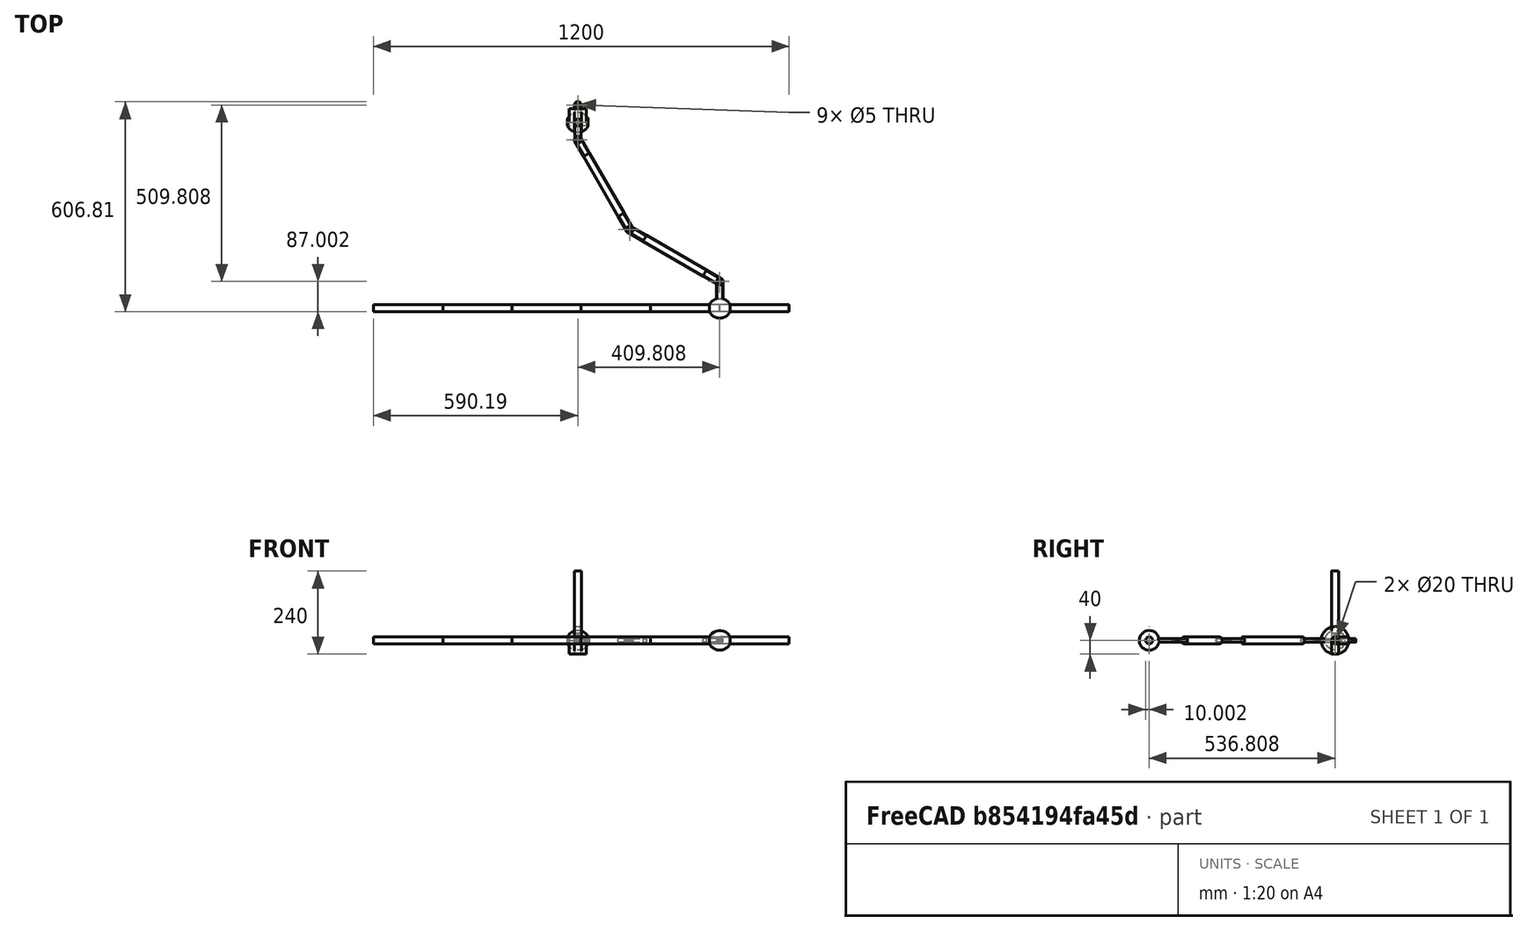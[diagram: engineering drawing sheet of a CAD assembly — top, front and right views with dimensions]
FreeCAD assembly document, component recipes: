
FREECAD ASSEMBLY — COMPONENT RECIPES ("Demo4Rev-Rev")

This assembly document has 7 components, labeled P0..P6 below (a component is one placed body or linked part). 7 of them carry a construction recipe — the FreeCAD feature program that regenerates the part from scratch, quoted from this document or its linked companion documents; the rest are supplied as boundary geometry only. No exploded tour is included for this assembly.
COMPONENT P0 — recipe-attached ("Weight", modeled in this document).
Construction recipe (the document's own serialized feature program — sketch geometry with constraints, then the solid features built on it; lengths are millimeters unless a unit is written):

FEATURE [Sketcher::SketchObject] Sketch
  FullyConstrained = true
  MapMode = 5
  Support = -> [XY_Plane]
  sketch-geometry (2):
    g0: LineSegment StartX=-30 StartY=10 StartZ=0 EndX=30 EndY=10 EndZ=0
    g1: ArcOfCircle CenterX=0 CenterY=-5 CenterZ=0 NormalX=0 NormalY=0 NormalZ=1 AngleXU=0 Radius=33.541 StartAngle=0.463648 EndAngle=2.67795
  constraints (7):
    c: Horizontal(g0)
    c: DistanceY(g-1,g0) = 10
    c: DistanceX(g-1,g0) = 30
    c: PointOnObject(g1,g-2)
    c: DistanceY(g1,g-1) = 5
    c: Coincident(g1,g0)
    c: Coincident(g1,g0)
FEATURE [PartDesign::Revolution] Revolution
  Angle = 360
  Axis = (1,0,0)
  Base = (0,0,0)
  Profile = -> Sketch
  ReferenceAxis = -> Sketch [H_Axis]
FEATURE [PartDesign::CoordinateSystem] WeightTop
  AttacherType = Attacher::AttachEngine3D
  MapMode = 11
  Placement = pos=(30,-1.8e-15,0) rot=(0.707107,0,0.707107;3.14159rad)
  Support = -> [Revolution]
FEATURE [PartDesign::CoordinateSystem] WeightBot
  AttacherType = Attacher::AttachEngine3D
  MapMode = 11
  Placement = pos=(-30,0,0) rot=(0.707107,0,0.707107;3.14159rad)
  Support = -> [Revolution]
FEATURE [PartDesign::CoordinateSystem] WeightLCS
  AttacherType = Attacher::AttachEngine3D
  MapMode = 2
  Support = -> [Body003]
FEATURE [PartDesign::Body] Body  label="Weight"
  Group = -> [Sketch,Revolution,WeightLCS,WeightTop,WeightBot]
  Origin = -> Origin
  Tip = -> Revolution
COMPONENT P1 — recipe-attached ("Rod", modeled in this document).
Construction recipe (the document's own serialized feature program — sketch geometry with constraints, then the solid features built on it; lengths are millimeters unless a unit is written):

FEATURE [Sketcher::SketchObject] Sketch001
  FullyConstrained = true
  MapMode = 5
  Support = -> [XY_Plane001]
  sketch-geometry (1):
    g0: Circle CenterX=0 CenterY=0 CenterZ=0 NormalX=0 NormalY=0 NormalZ=1 AngleXU=0 Radius=10
  constraints (2):
    c: Coincident(g0,g-1)
    c: Diameter(g0) = 20
FEATURE [PartDesign::Pad] Pad
  Direction = (0,0,1)
  Length = 200
  Length2 = 10
  Profile = -> Sketch001
  ReferenceAxis = -> Sketch001 [N_Axis]
  Type = 0
FEATURE [PartDesign::CoordinateSystem] RodTop
  AttacherType = Attacher::AttachEngine3D
  MapMode = 11
  Placement = pos=(0,0,200) rot=(0,0,1;1.5708rad)
  Support = -> [Pad]
FEATURE [PartDesign::CoordinateSystem] RodBottom
  AttacherType = Attacher::AttachEngine3D
  MapMode = 11
  Placement = pos=(0,0,0) rot=(0,0,1;1.5708rad)
  Support = -> [Pad]
FEATURE [PartDesign::Body] Body001  label="Rod"
  Group = -> [Sketch001,Pad,RodTop,RodBottom]
  Origin = -> Origin001
  Tip = -> Pad
COMPONENT P2 — recipe-attached ("LugBody", modeled in this document).
Construction recipe (the document's own serialized feature program — sketch geometry with constraints, then the solid features built on it; lengths are millimeters unless a unit is written):

FEATURE [Sketcher::SketchObject] Sketch002
  FullyConstrained = true
  MapMode = 5
  Support = -> [XY_Plane002]
  sketch-geometry (5):
    g0: LineSegment StartX=-10 StartY=0 StartZ=0 EndX=-10 EndY=50 EndZ=0
    g1: ArcOfCircle CenterX=0 CenterY=50 CenterZ=0 NormalX=0 NormalY=0 NormalZ=1 AngleXU=0 Radius=10 StartAngle=1e-16 EndAngle=3.14159
    g2: LineSegment StartX=10 StartY=50 StartZ=0 EndX=10 EndY=0 EndZ=0
    g3: LineSegment StartX=10 StartY=0 StartZ=0 EndX=-10 EndY=0 EndZ=0
    g4: Circle CenterX=0 CenterY=50 CenterZ=0 NormalX=0 NormalY=0 NormalZ=1 AngleXU=0 Radius=2.5
  constraints (13):
    c: PointOnObject(g0,g-1)
    c: Vertical(g0)
    c: Tangent(g0,g1) = 1.5708
    c: Tangent(g1,g2) = 1.5708
    c: Coincident(g2,g3)
    c: Coincident(g3,g0)
    c: Horizontal(g3)
    c: PointOnObject(g1,g-2)
    c: Vertical(g2)
    c: Diameter(g1) = 20
    c: Distance(g2) = 50
    c: Coincident(g4,g1)
    c: Diameter(g4) = 5
FEATURE [PartDesign::Pad] Pad001
  Direction = (0,0,1)
  Length = 10
  Length2 = 10
  Midplane = true
  Profile = -> Sketch002
  ReferenceAxis = -> Sketch002 [N_Axis]
  Type = 0
FEATURE [PartDesign::Body] Body002  label="LugBody"
  Group = -> [Sketch002,Pad001]
  Origin = -> Origin002
  Tip = -> Pad001
COMPONENT P3 — recipe-attached ("LugCylinder", modeled in this document).
Construction recipe (the document's own serialized feature program — sketch geometry with constraints, then the solid features built on it; lengths are millimeters unless a unit is written):

FEATURE [Sketcher::SketchObject] Sketch003
  FullyConstrained = true
  MapMode = 5
  Placement = pos=(0,0,0) rot=(1,0,0;1.5708rad)
  Support = -> [XZ_Plane003]
  sketch-geometry (1):
    g0: Circle CenterX=0 CenterY=0 CenterZ=0 NormalX=0 NormalY=0 NormalZ=1 AngleXU=0 Radius=10
  constraints (2):
    c: Coincident(g0,g-1)
    c: Diameter(g0) = 20
FEATURE [PartDesign::Pad] Pad002
  Direction = (0,-1,-2e-16)
  Length = 60
  Length2 = 10
  Placement = pos=(0,0,0) rot=(1,0,0;1.5708rad)
  Profile = -> Sketch003
  ReferenceAxis = -> Sketch003 [N_Axis]
  Reversed = true
  Type = 0
FEATURE [PartDesign::Boolean] Boolean
  BaseFeature = -> Pad002
  Group = -> [Body002]
  Type = 2
FEATURE [PartDesign::CoordinateSystem] LugHole
  AttacherType = Attacher::AttachEngine3D
  MapMode = 11
  Placement = pos=(0,50,5) rot=(0,0,1;1.5708rad)
  Support = -> [Boolean]
FEATURE [PartDesign::CoordinateSystem] LugFace
  AttacherType = Attacher::AttachEngine3D
  MapMode = 5
  Placement = pos=(0,0,0) rot=(1,0,0;1.5708rad)
  Support = -> [Boolean]
FEATURE [PartDesign::CoordinateSystem] LugRot30
  AttacherType = Attacher::AttachEngine3D
  AttachmentOffset = pos=(0,0,0) rot=(0,0,1;0.523599rad)
  MapMode = 11
  Placement = pos=(0,50,5) rot=(0,0,1;2.0944rad)
  Support = -> [Boolean]
FEATURE [PartDesign::CoordinateSystem] LugRot60
  AttacherType = Attacher::AttachEngine3D
  AttachmentOffset = pos=(0,0,0) rot=(0,0,1;1.0472rad)
  MapMode = 11
  Placement = pos=(0,50,5) rot=(0,0,1;2.61799rad)
  Support = -> [Boolean]
FEATURE [PartDesign::Body] Body003  label="LugCylinder"
  Group = -> [Sketch003,Pad002,Boolean,LugHole,LugFace,LugRot30,LugRot60]
  Origin = -> Origin003
  Tip = -> Boolean
COMPONENT P4 — recipe-attached ("BobBody", modeled in this document).
Construction recipe (the document's own serialized feature program — sketch geometry with constraints, then the solid features built on it; lengths are millimeters unless a unit is written):

FEATURE [Sketcher::SketchObject] Sketch004
  FullyConstrained = true
  MapMode = 5
  Support = -> [XY_Plane004]
  sketch-geometry (4):
    g0: LineSegment StartX=-10 StartY=0 StartZ=0 EndX=-10 EndY=30 EndZ=0
    g1: ArcOfCircle CenterX=0 CenterY=30 CenterZ=0 NormalX=0 NormalY=0 NormalZ=1 AngleXU=0 Radius=10 StartAngle=2e-16 EndAngle=3.14159
    g2: LineSegment StartX=10 StartY=30 StartZ=0 EndX=10 EndY=0 EndZ=0
    g3: LineSegment StartX=10 StartY=0 StartZ=0 EndX=-10 EndY=0 EndZ=0
  constraints (11):
    c: PointOnObject(g0,g-1)
    c: Vertical(g0)
    c: Tangent(g0,g1) = 1.5708
    c: Tangent(g1,g2) = 1.5708
    c: Coincident(g2,g3)
    c: Coincident(g3,g0)
    c: Vertical(g2)
    c: PointOnObject(g1,g-2)
    c: Diameter(g1) = 20
    c: Distance(g0) = 30
    c: PointOnObject(g2,g-1)
FEATURE [PartDesign::Revolution] Revolution001
  Angle = 360
  Axis = (1,0,0)
  Base = (0,0,0)
  Profile = -> Sketch004
  ReferenceAxis = -> Sketch004 [H_Axis]
FEATURE [PartDesign::CoordinateSystem] BobBody  label="BobBody001"
  AttacherType = Attacher::AttachEngine3D
  MapMode = 11
  Placement = pos=(-10,0,0) rot=(0.707107,0,0.707107;3.14159rad)
  Support = -> [Revolution001]
FEATURE [PartDesign::Body] Body004  label="BobBody"
  Group = -> [Sketch004,Revolution001,BobBody]
  Origin = -> Origin004
  Tip = -> Revolution001
COMPONENT P5 — recipe-attached ("GroundBody", modeled in this document).
Construction recipe (the document's own serialized feature program — sketch geometry with constraints, then the solid features built on it; lengths are millimeters unless a unit is written):

FEATURE [Sketcher::SketchObject] Sketch005
  FullyConstrained = true
  MapMode = 5
  Support = -> [XY_Plane005]
  sketch-geometry (4):
    g0: LineSegment StartX=-25 StartY=10 StartZ=0 EndX=25 EndY=10 EndZ=0
    g1: LineSegment StartX=25 StartY=10 StartZ=0 EndX=25 EndY=-10 EndZ=0
    g2: LineSegment StartX=25 StartY=-10 StartZ=0 EndX=-25 EndY=-10 EndZ=0
    g3: LineSegment StartX=-25 StartY=-10 StartZ=0 EndX=-25 EndY=10 EndZ=0
  constraints (11):
    c: Coincident(g0,g1)
    c: Coincident(g1,g2)
    c: Coincident(g2,g3)
    c: Coincident(g3,g0)
    c: Horizontal(g0)
    c: Horizontal(g2)
    c: Vertical(g1)
    c: Vertical(g3)
    c: DistanceY(g2,g0) = 20
    c: DistanceX(g0,g0) = 50
    c: Symmetric(g0,g1,g-1)
FEATURE [PartDesign::Pad] Pad003
  Direction = (0,0,1)
  Length = 40
  Length2 = 10
  Profile = -> Sketch005
  ReferenceAxis = -> Sketch005 [N_Axis]
  Reversed = true
  Type = 0
FEATURE [PartDesign::CoordinateSystem] GroundLCS
  AttacherType = Attacher::AttachEngine3D
  MapMode = 5
  Placement = pos=(0,0,-40) rot=(1,0,0;3.14159rad)
  Support = -> [Pad003]
FEATURE [PartDesign::Body] Body005  label="GroundBody"
  Group = -> [Sketch005,Pad003,GroundLCS]
  Origin = -> Origin005
  Tip = -> Pad003
COMPONENT P6 — recipe-attached ("Spacer", modeled in this document).
Construction recipe (the document's own serialized feature program — sketch geometry with constraints, then the solid features built on it; lengths are millimeters unless a unit is written):

FEATURE [Sketcher::SketchObject] Sketch006
  FullyConstrained = true
  MapMode = 5
  Support = -> [XY_Plane007]
  sketch-geometry (2):
    g0: Circle CenterX=0 CenterY=0 CenterZ=0 NormalX=0 NormalY=0 NormalZ=1 AngleXU=0 Radius=10
    g1: Circle CenterX=0 CenterY=0 CenterZ=0 NormalX=0 NormalY=0 NormalZ=1 AngleXU=0 Radius=2.5
  constraints (4):
    c: Coincident(g0,g-1)
    c: Coincident(g1,g0)
    c: Diameter(g0) = 20
    c: Diameter(g1) = 5
FEATURE [PartDesign::Pad] Pad004
  Direction = (0,0,1)
  Length = 20
  Length2 = 10
  Profile = -> Sketch006
  ReferenceAxis = -> Sketch006 [N_Axis]
  Type = 0
FEATURE [PartDesign::CoordinateSystem] SpacerTop
  AttacherType = Attacher::AttachEngine3D
  MapMode = 11
  Placement = pos=(0,0,20) rot=(0,0,1;1.5708rad)
  Support = -> [Pad004]
FEATURE [PartDesign::Body] Body006  label="Spacer"
  Group = -> [Sketch006,Pad004,SpacerTop]
  Origin = -> Origin007
  Tip = -> Pad004
PROVENANCE & LICENSES
A FreeCAD (.FCStd) document from a public repository crawl; recipes are the document's own serialized feature recipes (and, for linked parts, companion documents' recipes).
License: gpl-3.0.
